# Revit family: SIGNUM Dämmgummi LP50
name_source: partatom
category: HLS-Bauteile
units: mm (PartAtom-declared; Revit-internal decimal feet)

## family parameters
Arbeitsebenenbasiert = Ja
Beim Laden mit Abzugskörper schneiden = Nein
Bemaßung runder Anschluss = Durchmesser verwenden
Beschriftungsausrichtung beibehalten = Nein
Gemeinsam genutzt = Ja
Immer vertikal = Nein
Klassifizierung = Keine
Raumberechnungspunkt = Nein
Teiletyp = Normal

## types (1)
- SIGNUM Dämmgummi LP50
    Artikelnummer = 72102032
    Breite = 25 mm  [stored 0.082021 ft]
    Dämmstärke = 3 mm  [stored 0.00984252 ft]
    EAN = 4250928467898
    Fabrikat = MEFA
    Farbe = Schwarz
    Gewicht = 0,12 kg
    Kurztext1 = SIGNUM Dämmgummi LP50
    Kurztext2 = 10 m Gummi
    Länge = 10000 mm
    Material = Gummi
    Materialname = EPDM
    Mengeneinheit = m
    Profiltyp = LP50
    Stärke = 3 mm  [stored 0.00984252 ft]
    Vorgabe-Ansicht = 1219 mm
    max. Temperaturbeständigkeit = 100 °C
    vpe = 10

note: [stored X ft] marks values corroborated as IEEE doubles in the binary element streams (Revit-internal decimal feet)
